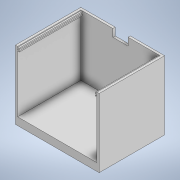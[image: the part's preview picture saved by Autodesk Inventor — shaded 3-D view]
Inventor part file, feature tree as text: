
AUTODESK INVENTOR PART (.ipt)
format: ipt  version: 2022 (Build 260153000, 153)  size: 155,648 bytes
history: native  units: mm
features: extrude x5, sketch x5
ambient origin geometry x8: Origin, YZ Plane, XZ Plane, XY Plane, X Axis, Y Axis, Z Axis, Center Point
bodies: Body1 (feature_tree)
feature tree (10):
  extrude  "Extrusion6"  Depth=86.0mm
  extrude  "Extrusion7"  Depth=80.0mm TaperAngle=0.0deg
  extrude  "Extrusion8"  Depth=10.0mm
  extrude  "Extrusion9"  Depth=80.0mm TaperAngle=0.0deg
  extrude  "Extrusion10"  Depth=1.5mm
  sketch  "Sketch12"  dims[d23=110.0mm d24=86.0mm]
  sketch  "Sketch13"  dims[d25=10.0mm d26=0.0mm d30=80.0mm d31=0.0mm]
  sketch  "Sketch14"  dims[d33=20.0mm d34=10.0mm]
  sketch  "Sketch15"  dims[d35=20.0mm d36=80.0mm d37=0.0mm]
  sketch  "Sketch16"  dims[d39=1.5mm d40=1.5mm d41=1.5mm d42=2.0mm d43=0.0mm d45=1.5mm d46=1.5mm d47=1.5mm d48=2.0mm d49=0.0mm]
